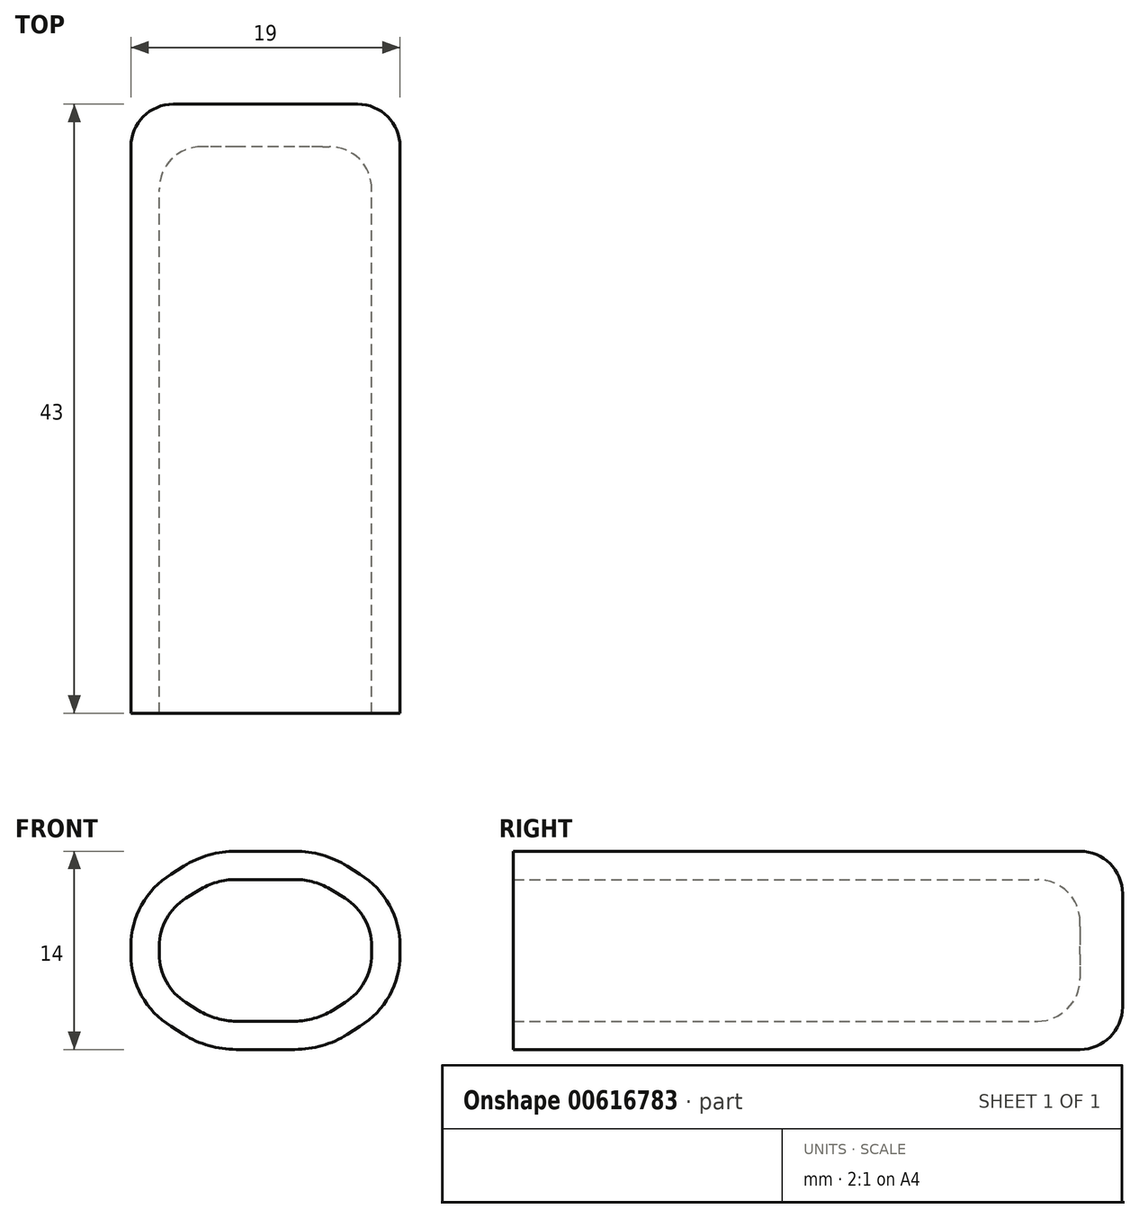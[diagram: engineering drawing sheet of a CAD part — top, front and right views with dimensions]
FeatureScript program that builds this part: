
annotation { "Feature Type Name" : "Feature", "Feature Type Description" : "" }
export const myFeature = defineFeature(function(context is Context, id is Id, definition is map)
    precondition{}
    {
        {
            var Q0;
            Q0=qCreatedBy(makeId("Front.planeOp"),FACE);
            var sketch = newSketch(context, id + "F0", { "sketchPlane" : qUnion([Q0])});
            skLineSegment(sketch, "E0.bottom", {"start": v(2.07, -5) * mm, "end": v(-2.07, -5) * mm});
            skLineSegment(sketch, "E0.top", {"start": v(2.07, 5) * mm, "end": v(-2.07, 5) * mm});
            skLineSegment(sketch, "E0.left", {"start": v(7.5, -0.28) * mm, "end": v(7.5, 0.28) * mm});
            skLineSegment(sketch, "E0.right", {"start": v(-7.5, -0.28) * mm, "end": v(-7.5, 0.28) * mm});
            skPoint(sketch, "E0.middle", {"position": v(0, 0) * mm});
            skLineSegment(sketch, "E1", {"start": v(-4.72, 4.24) * mm, "end": v(-5.62, 3.68) * mm});
            skLineSegment(sketch, "E2", {"start": v(-5.62, -3.68) * mm, "end": v(-4.72, -4.24) * mm});
            skLineSegment(sketch, "E3.MirrorCS", {"start": v(4.72, 4.24) * mm, "end": v(5.62, 3.68) * mm});
            skLineSegment(sketch, "E4.MirrorCS", {"start": v(5.62, -3.68) * mm, "end": v(4.72, -4.24) * mm});
            skPoint(sketch, "E5.orphan", {"position": v(-7.5, 5) * mm});
            skPoint(sketch, "E6.orphan", {"position": v(-7.5, -5) * mm});
            skPoint(sketch, "E7.orphan", {"position": v(7.5, -5) * mm});
            skPoint(sketch, "E8.orphan", {"position": v(7.5, 5) * mm});
            skPoint(sketch, "E9.visualSharp", {"position": v(-7.5, 2.5) * mm});
            skArc(sketch, "E9.filletArc", {"start": v(-5.62, 3.68) * mm, "mid": v(-7, 2.22) * mm, "end": v(-7.5, 0.28) * mm});
            skPoint(sketch, "E10.visualSharp", {"position": v(-7.5, -2.5) * mm});
            skArc(sketch, "E10.filletArc", {"start": v(-7.5, -0.28) * mm, "mid": v(-7, -2.22) * mm, "end": v(-5.62, -3.68) * mm});
            skPoint(sketch, "E11.visualSharp", {"position": v(7.5, -2.5) * mm});
            skArc(sketch, "E11.filletArc", {"start": v(5.62, -3.68) * mm, "mid": v(7, -2.22) * mm, "end": v(7.5, -0.28) * mm});
            skPoint(sketch, "E12.visualSharp", {"position": v(7.5, 2.5) * mm});
            skArc(sketch, "E12.filletArc", {"start": v(7.5, 0.28) * mm, "mid": v(7, 2.22) * mm, "end": v(5.62, 3.68) * mm});
            skPoint(sketch, "E13.visualSharp", {"position": v(-3.5, 5) * mm});
            skArc(sketch, "E13.filletArc", {"start": v(-2.07, 5) * mm, "mid": v(-3.44, 4.8) * mm, "end": v(-4.72, 4.24) * mm});
            skPoint(sketch, "E14.visualSharp", {"position": v(3.5, 5) * mm});
            skArc(sketch, "E14.filletArc", {"start": v(4.72, 4.24) * mm, "mid": v(3.44, 4.8) * mm, "end": v(2.07, 5) * mm});
            skPoint(sketch, "E15.visualSharp", {"position": v(-3.5, -5) * mm});
            skArc(sketch, "E15.filletArc", {"start": v(-4.72, -4.24) * mm, "mid": v(-3.44, -4.8) * mm, "end": v(-2.07, -5) * mm});
            skPoint(sketch, "E16.visualSharp", {"position": v(3.5, -5) * mm});
            skArc(sketch, "E16.filletArc", {"start": v(2.07, -5) * mm, "mid": v(3.44, -4.8) * mm, "end": v(4.72, -4.24) * mm});
            skSolve(sketch);
        }
        {
            var Q0;
            Q0=makeQuery(id+"F0.imprint","IMPRINT",FACE,{"disambiguationData":[TD([[makeQuery(id+"F0.imprint","IMPRINT",EDGE,{"derivedFrom":sQuery(id+"F0.wireOp",EDGE,"E0.bottom")}),-1.0]])]});
            extrude(context, id + "F1", {"entities" : qUnion([Q0]), "depth" : 40 * mm, "offsetDistance" : 25 * mm});
        }
        {
            var Q0;
            Q0=makeQuery(id+"F1.opExtrude","CAP_FACE",FACE,{"disambiguationData":[OSD([sQuery(id+"F0.wireOp",EDGE,"E0.bottom"),sQuery(id+"F0.wireOp",EDGE,"E0.top"),sQuery(id+"F0.wireOp",EDGE,"E0.left"),sQuery(id+"F0.wireOp",EDGE,"E0.right"),sQuery(id+"F0.wireOp",EDGE,"E1"),sQuery(id+"F0.wireOp",EDGE,"E2"),sQuery(id+"F0.wireOp",EDGE,"E3.MirrorCS"),sQuery(id+"F0.wireOp",EDGE,"E4.MirrorCS"),sQuery(id+"F0.wireOp",EDGE,"E9.filletArc"),sQuery(id+"F0.wireOp",EDGE,"E10.filletArc"),sQuery(id+"F0.wireOp",EDGE,"E11.filletArc"),sQuery(id+"F0.wireOp",EDGE,"E12.filletArc"),sQuery(id+"F0.wireOp",EDGE,"E13.filletArc"),sQuery(id+"F0.wireOp",EDGE,"E14.filletArc"),sQuery(id+"F0.wireOp",EDGE,"E15.filletArc"),sQuery(id+"F0.wireOp",EDGE,"E16.filletArc")])],"isStart":false});
            shell(context, id + "F2", {"entities" : qUnion([Q0]), "thickness" : 2 * mm, "oppositeDirection" : true});
        }
        {
            var Q0;
            Q0=makeQuery(id+"F1.opExtrude","CAP_FACE",FACE,{"disambiguationData":[OSD([sQuery(id+"F0.wireOp",EDGE,"E0.bottom"),sQuery(id+"F0.wireOp",EDGE,"E0.top"),sQuery(id+"F0.wireOp",EDGE,"E0.left"),sQuery(id+"F0.wireOp",EDGE,"E0.right"),sQuery(id+"F0.wireOp",EDGE,"E1"),sQuery(id+"F0.wireOp",EDGE,"E2"),sQuery(id+"F0.wireOp",EDGE,"E3.MirrorCS"),sQuery(id+"F0.wireOp",EDGE,"E4.MirrorCS"),sQuery(id+"F0.wireOp",EDGE,"E9.filletArc"),sQuery(id+"F0.wireOp",EDGE,"E10.filletArc"),sQuery(id+"F0.wireOp",EDGE,"E11.filletArc"),sQuery(id+"F0.wireOp",EDGE,"E12.filletArc"),sQuery(id+"F0.wireOp",EDGE,"E13.filletArc"),sQuery(id+"F0.wireOp",EDGE,"E14.filletArc"),sQuery(id+"F0.wireOp",EDGE,"E15.filletArc"),sQuery(id+"F0.wireOp",EDGE,"E16.filletArc")])],"isStart":true});
            extrude(context, id + "F3", {"entities" : qUnion([Q0]), "operationType" : NewBodyOperationType.ADD, "depth" : 1 * mm, "offsetDistance" : 25 * mm});
        }
        {
            var Q0;
            Q0=makeQuery(id+"F3.opExtrude","CAP_FACE",FACE,{"disambiguationData":[OSD([sQuery(id+"F0.wireOp",EDGE,"E0.bottom"),sQuery(id+"F0.wireOp",EDGE,"E0.top"),sQuery(id+"F0.wireOp",EDGE,"E0.left"),sQuery(id+"F0.wireOp",EDGE,"E0.right"),sQuery(id+"F0.wireOp",EDGE,"E1"),sQuery(id+"F0.wireOp",EDGE,"E2"),sQuery(id+"F0.wireOp",EDGE,"E3.MirrorCS"),sQuery(id+"F0.wireOp",EDGE,"E4.MirrorCS"),sQuery(id+"F0.wireOp",EDGE,"E9.filletArc"),sQuery(id+"F0.wireOp",EDGE,"E10.filletArc"),sQuery(id+"F0.wireOp",EDGE,"E11.filletArc"),sQuery(id+"F0.wireOp",EDGE,"E12.filletArc"),sQuery(id+"F0.wireOp",EDGE,"E13.filletArc"),sQuery(id+"F0.wireOp",EDGE,"E14.filletArc"),sQuery(id+"F0.wireOp",EDGE,"E15.filletArc"),sQuery(id+"F0.wireOp",EDGE,"E16.filletArc")])],"isStart":false});
            var Q1;
            Q1=makeQuery(id+"F2.opShell","OFFSET_FACE",FACE,{"disambiguationData":[OSD([sQuery(id+"F0.wireOp",EDGE,"E0.bottom"),sQuery(id+"F0.wireOp",EDGE,"E0.top"),sQuery(id+"F0.wireOp",EDGE,"E0.left"),sQuery(id+"F0.wireOp",EDGE,"E0.right"),sQuery(id+"F0.wireOp",EDGE,"E1"),sQuery(id+"F0.wireOp",EDGE,"E2"),sQuery(id+"F0.wireOp",EDGE,"E3.MirrorCS"),sQuery(id+"F0.wireOp",EDGE,"E4.MirrorCS"),sQuery(id+"F0.wireOp",EDGE,"E9.filletArc"),sQuery(id+"F0.wireOp",EDGE,"E10.filletArc"),sQuery(id+"F0.wireOp",EDGE,"E11.filletArc"),sQuery(id+"F0.wireOp",EDGE,"E12.filletArc"),sQuery(id+"F0.wireOp",EDGE,"E13.filletArc"),sQuery(id+"F0.wireOp",EDGE,"E14.filletArc"),sQuery(id+"F0.wireOp",EDGE,"E15.filletArc"),sQuery(id+"F0.wireOp",EDGE,"E16.filletArc")])]});
            fillet(context, id + "F4", {"entities" : qUnion([Q0, Q1]), "radius" : 3 * mm, "allowEdgeOverflow" : false});
        }
    });
